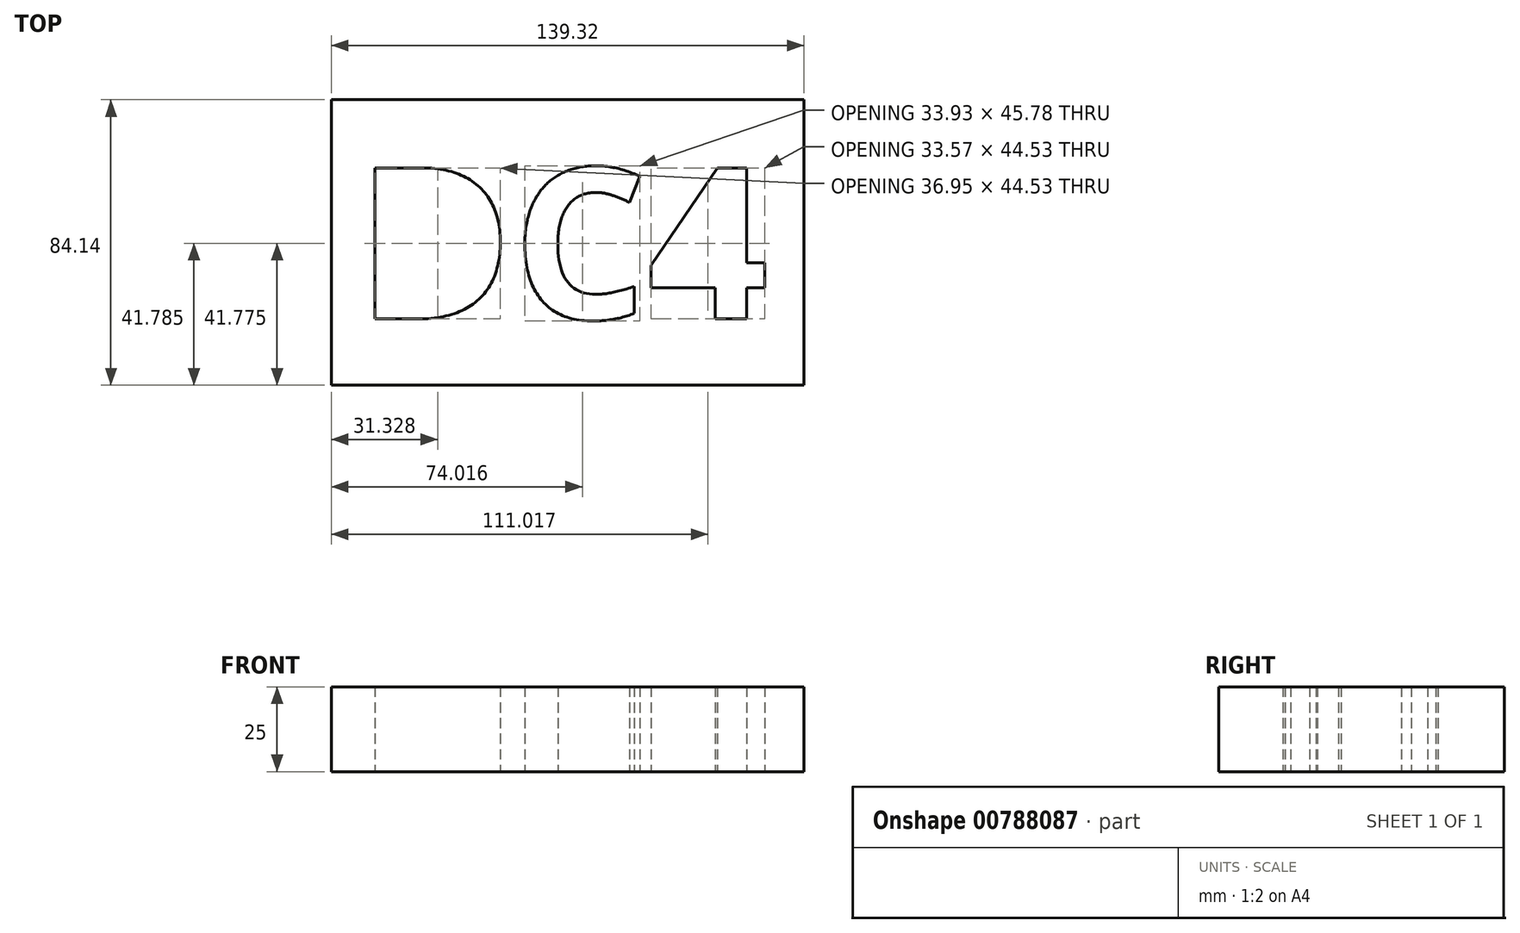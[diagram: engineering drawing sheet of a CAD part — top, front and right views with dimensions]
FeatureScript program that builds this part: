
annotation { "Feature Type Name" : "Feature", "Feature Type Description" : "" }
export const myFeature = defineFeature(function(context is Context, id is Id, definition is map)
    precondition{}
    {
        {
            var Q0;
            Q0=qCreatedBy(makeId("Top.planeOp"),FACE);
            var sketch = newSketch(context, id + "F0", { "sketchPlane" : qUnion([Q0])});
            skLineSegment(sketch, "E0.bottom", {"start": v(69.66, 42.06) * mm, "end": v(-69.66, 42.06) * mm});
            skLineSegment(sketch, "E0.top", {"start": v(69.66, -42.06) * mm, "end": v(-69.66, -42.06) * mm});
            skLineSegment(sketch, "E0.left", {"start": v(69.66, 42.06) * mm, "end": v(69.66, -42.06) * mm});
            skLineSegment(sketch, "E0.right", {"start": v(-69.66, 42.06) * mm, "end": v(-69.66, -42.06) * mm});
            skPoint(sketch, "E0.middle", {"position": v(0, 0) * mm});
            skText(sketch, "E1", { "text": "DC4", "fontName": "OpenSans-Bold.ttf"});
            const initialGuessF0  = {"E1": [-0.06241, -0.02256, 1, 0, 0.04491]};
            skSetInitialGuess(sketch, initialGuessF0);
            skSolve(sketch);
        }
        {
            var Q0;
            Q0 = qSketchRegion(id + "F0", true);
            extrude(context, id + "F1", {"entities" : qUnion([Q0]), "depth" : 25 * mm, "offsetDistance" : 25 * mm});
        }
    });
